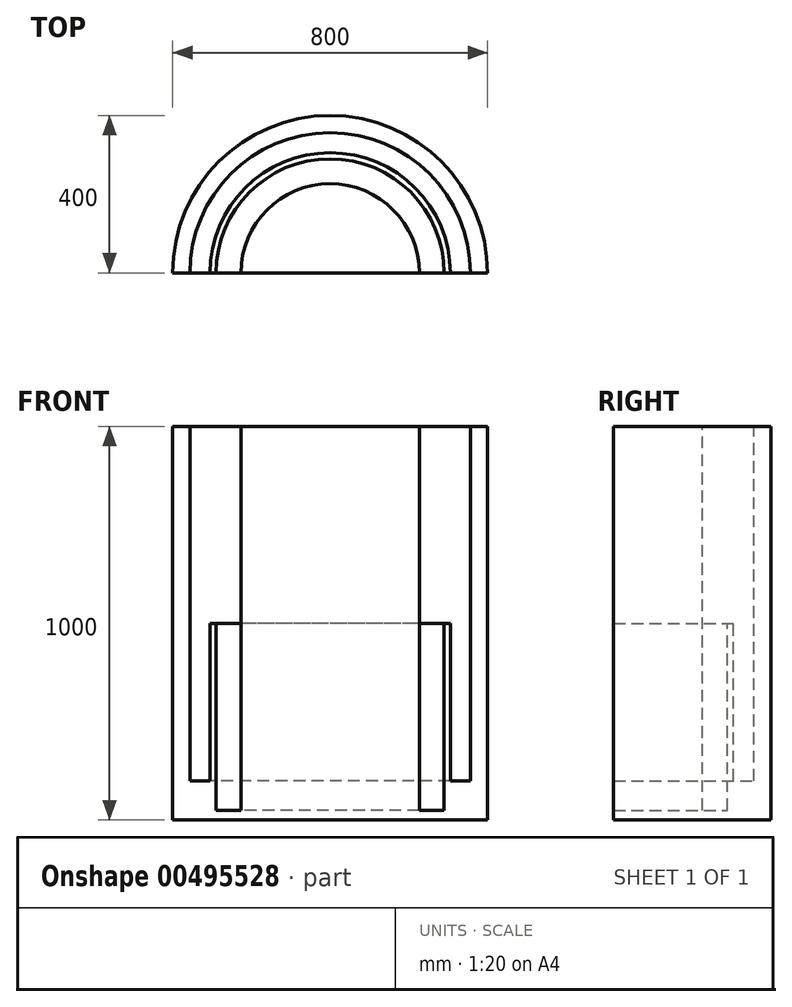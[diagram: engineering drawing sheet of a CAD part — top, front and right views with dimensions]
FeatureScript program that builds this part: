
annotation { "Feature Type Name" : "Feature", "Feature Type Description" : "" }
export const myFeature = defineFeature(function(context is Context, id is Id, definition is map)
    precondition{}
    {
        {
            var Q0;
            Q0=qCreatedBy(makeId("Front.planeOp"),FACE);
            var sketch = newSketch(context, id + "F0", { "sketchPlane" : qUnion([Q0])});
            skLineSegment(sketch, "E0", {"start": v(0, 0) * mm, "end": v(0, 1000) * mm});
            skLineSegment(sketch, "E1", {"start": v(0, 0) * mm, "end": v(400, 0) * mm});
            skLineSegment(sketch, "E2", {"start": v(0, 1000) * mm, "end": v(226.55, 1000) * mm});
            skLineSegment(sketch, "E3", {"start": v(226.55, 1000) * mm, "end": v(226.55, 25) * mm});
            skLineSegment(sketch, "E4", {"start": v(356.3, 100) * mm, "end": v(356.3, 1000) * mm});
            skLineSegment(sketch, "E5", {"start": v(400, 0) * mm, "end": v(400, 1000) * mm});
            skLineSegment(sketch, "E6", {"start": v(400, 1000) * mm, "end": v(356.3, 1000) * mm});
            skLineSegment(sketch, "E7", {"start": v(356.3, 100) * mm, "end": v(305.3, 100) * mm});
            skLineSegment(sketch, "E8", {"start": v(305.3, 100) * mm, "end": v(305.3, 500) * mm});
            skLineSegment(sketch, "E9", {"start": v(305.3, 500) * mm, "end": v(289.8, 500) * mm});
            skLineSegment(sketch, "E10", {"start": v(289.8, 500) * mm, "end": v(289.8, 25) * mm});
            skLineSegment(sketch, "E11", {"start": v(226.55, 25) * mm, "end": v(289.8, 25) * mm});
            skSolve(sketch);
        }
        {
            var Q0;
            Q0 = qSketchRegion(id + "F0", true);
            var Q1;
            Q1=sQuery(id+"F0.wireOp",EDGE,"E0");
            revolve(context, id + "F1", {"entities" : qUnion([Q0]), "axis" : qUnion([Q1]), "revolveType" : RevolveType.TWO_DIRECTIONS, "oppositeDirection" : true, "angle" : 0 * degree, "angleBack" : 180 * degree});
        }
    });
